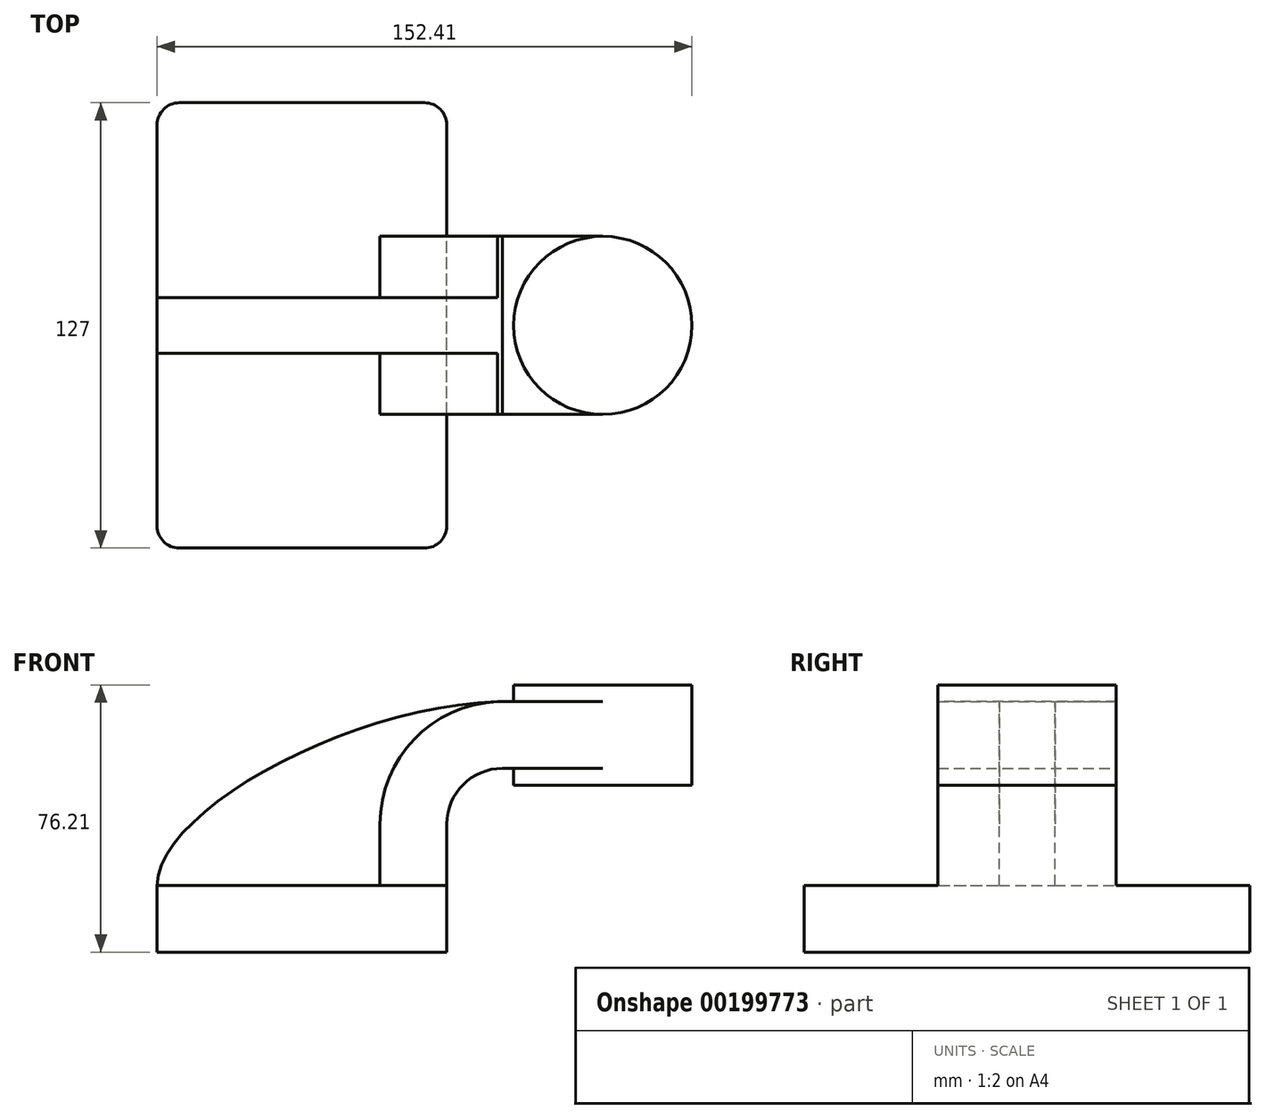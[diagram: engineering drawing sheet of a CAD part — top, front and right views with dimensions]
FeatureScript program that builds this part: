
annotation { "Feature Type Name" : "Feature", "Feature Type Description" : "" }
export const myFeature = defineFeature(function(context is Context, id is Id, definition is map)
    precondition{}
    {
        {
            var Q0;
            Q0=qCreatedBy(makeId("Front.planeOp"),FACE);
            var sketch = newSketch(context, id + "F0", { "sketchPlane" : qUnion([Q0])});
            skLineSegment(sketch, "E0.bottom", {"start": v(-41.28, 9.52) * mm, "end": v(41.27, 9.53) * mm});
            skLineSegment(sketch, "E0.top", {"start": v(-41.28, -9.53) * mm, "end": v(41.28, -9.53) * mm});
            skLineSegment(sketch, "E0.left", {"start": v(-41.28, 9.52) * mm, "end": v(-41.28, -9.53) * mm});
            skLineSegment(sketch, "E0.right", {"start": v(41.28, 9.53) * mm, "end": v(41.28, -9.52) * mm});
            skPoint(sketch, "E0.middle", {"position": v(0, 0) * mm});
            skLineSegment(sketch, "E1", {"start": v(41.28, 9.53) * mm, "end": v(41.28, 27) * mm});
            skArc(sketch, "E2", {"start": v(41.28, 27) * mm, "mid": v(45.92, 38.23) * mm, "end": v(57.15, 42.88) * mm});
            skLineSegment(sketch, "E3.bottom", {"start": v(60.32, 66.67) * mm, "end": v(111.12, 66.67) * mm});
            skLineSegment(sketch, "E3.top", {"start": v(60.32, 38.1) * mm, "end": v(111.12, 38.1) * mm});
            skLineSegment(sketch, "E3.left", {"start": v(60.32, 66.67) * mm, "end": v(60.32, 38.1) * mm});
            skLineSegment(sketch, "E3.right", {"start": v(111.12, 66.67) * mm, "end": v(111.12, 38.1) * mm});
            skArc(sketch, "E4.1", {"start": v(22.23, 27) * mm, "mid": v(32.45, 51.7) * mm, "end": v(57.15, 61.93) * mm});
            skLineSegment(sketch, "E4.2", {"start": v(22.22, 9.53) * mm, "end": v(22.22, 27) * mm});
            skFitSpline(sketch, "E5", {"points": [v(-41.28, 9.52) * mm, v(57.15, 61.93) * mm], "startDerivative": vector(1.26, 65.75) * mm, "endDerivative": vector(126.49, 1.63) * mm});
            skLineSegment(sketch, "E6", {"start": v(57.15, 61.93) * mm, "end": v(85.72, 61.93) * mm});
            skLineSegment(sketch, "E7", {"start": v(85.72, 61.93) * mm, "end": v(85.72, 42.88) * mm});
            skLineSegment(sketch, "E8", {"start": v(85.72, 42.88) * mm, "end": v(57.15, 42.88) * mm});
            skLineSegment(sketch, "E9", {"start": v(85.72, 61.93) * mm, "end": v(85.72, 66.67) * mm});
            skLineSegment(sketch, "E10", {"start": v(85.72, 42.88) * mm, "end": v(85.72, 38.1) * mm});
            skSolve(sketch);
        }
        {
            var Q0;
            Q0=makeQuery(id+"F0.imprint","IMPRINT",FACE,{"disambiguationData":[TD([[makeQuery(id+"F0.imprint","IMPRINT",EDGE,{"derivedFrom":sQuery(id+"F0.wireOp",EDGE,"E0.top")}),1.0]])]});
            extrude(context, id + "F1", {"entities" : qUnion([Q0]), "endBound" : BoundingType.SYMMETRIC, "depth" : 127 * mm});
        }
        {
            var Q0;
            {var subQ11=sQuery(id+"F0.wireOp",EDGE,"E1");Q0=makeQuery(id+"F0.imprint","IMPRINT",FACE,{"disambiguationData":[TD([[makeQuery(id+"F0.imprint","IMPRINT",EDGE,{"derivedFrom":subQ11}),1.0]])]});}
            var Q1;
            {var subQ5=sQuery(id+"F0.wireOp",EDGE,"E7");Q1=makeQuery(id+"F0.imprint","IMPRINT",FACE,{"disambiguationData":[TD([[makeQuery(id+"F0.imprint","IMPRINT",EDGE,{"derivedFrom":subQ5}),-1.0]])]});}
            extrude(context, id + "F2", {"entities" : qUnion([Q0, Q1]), "operationType" : NewBodyOperationType.ADD, "endBound" : BoundingType.SYMMETRIC, "depth" : 50.8 * mm});
        }
        {
            var Q0;
            {var subQ3=sQuery(id+"F0.wireOp",EDGE,"E4.2");Q0=makeQuery(id+"F0.imprint","IMPRINT",FACE,{"disambiguationData":[TD([[makeQuery(id+"F0.imprint","IMPRINT",EDGE,{"derivedFrom":subQ3}),1.0]])]});}
            extrude(context, id + "F3", {"entities" : qUnion([Q0]), "operationType" : NewBodyOperationType.ADD, "endBound" : BoundingType.SYMMETRIC, "depth" : 15.88 * mm});
        }
        {
            var Q0;
            {var subQ0=sQuery(id+"F0.wireOp",EDGE,"E3.right");Q0=makeQuery(id+"F0.imprint","IMPRINT",FACE,{"disambiguationData":[TD([[makeQuery(id+"F0.imprint","IMPRINT",EDGE,{"derivedFrom":subQ0}),-1.0]])]});}
            var Q1;
            Q1=sQuery(id+"F0.wireOp",EDGE,"E7");
            revolve(context, id + "F4", {"operationType" : NewBodyOperationType.ADD, "entities" : qUnion([Q0]), "axis" : qUnion([Q1]), "revolveType" : RevolveType.FULL});
        }
        {
            var Q0;
            Q0=makeQuery(id+"F1.opExtrude","CAP_EDGE",EDGE,{"disambiguationData":[OSD([sQuery(id+"F0.wireOp",EDGE,"E0.right")])],"isStart":false});
            var Q1;
            Q1=makeQuery(id+"F1.opExtrude","CAP_EDGE",EDGE,{"disambiguationData":[OSD([sQuery(id+"F0.wireOp",EDGE,"E0.left")])],"isStart":false});
            var Q2;
            Q2=makeQuery(id+"F1.opExtrude","CAP_EDGE",EDGE,{"disambiguationData":[OSD([sQuery(id+"F0.wireOp",EDGE,"E0.left")])],"isStart":true});
            var Q3;
            Q3=makeQuery(id+"F1.opExtrude","CAP_EDGE",EDGE,{"disambiguationData":[OSD([sQuery(id+"F0.wireOp",EDGE,"E0.right")])],"isStart":true});
            fillet(context, id + "F5", {"entities" : qUnion([Q0, Q1, Q2, Q3]), "radius" : 6.35 * mm, "tangentPropagation" : true, "allowEdgeOverflow" : false});
        }
    });
